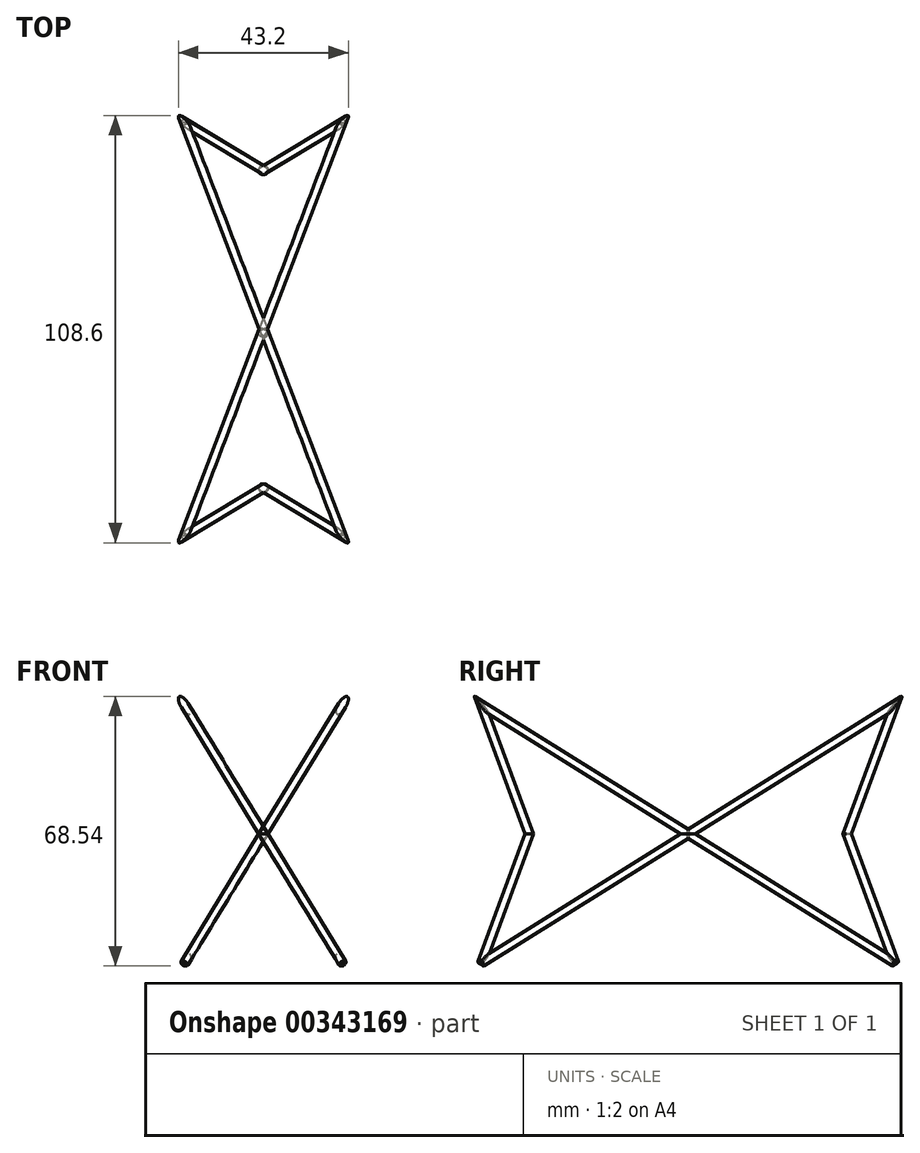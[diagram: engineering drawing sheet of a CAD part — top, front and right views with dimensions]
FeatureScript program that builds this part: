
annotation { "Feature Type Name" : "Feature", "Feature Type Description" : "" }
export const myFeature = defineFeature(function(context is Context, id is Id, definition is map)
    precondition{}
    {
        {
            var Q0;
            Q0=qCreatedBy(makeId("Right.planeOp"),FACE);
            var sketch = newSketch(context, id + "F0", { "sketchPlane" : qUnion([Q0])});
            skLineSegment(sketch, "E0", {"start": v(-52.44, 32.7) * mm, "end": v(52.44, -32.7) * mm, "construction": true});
            skLineSegment(sketch, "E1.MirrorCS", {"start": v(52.44, 32.7) * mm, "end": v(-52.44, -32.7) * mm, "construction": true});
            skLineSegment(sketch, "E2", {"start": v(-52.44, 32.7) * mm, "end": v(-40.37, 0) * mm, "construction": true});
            skLineSegment(sketch, "E3.MirrorCS", {"start": v(-52.44, -32.7) * mm, "end": v(-40.37, 0) * mm, "construction": true});
            skLineSegment(sketch, "E4.MirrorCS", {"start": v(52.44, 32.7) * mm, "end": v(40.37, 0) * mm, "construction": true});
            skLineSegment(sketch, "E5.MirrorCS", {"start": v(52.44, -32.7) * mm, "end": v(40.37, 0) * mm, "construction": true});
            skSolve(sketch);
        }
        {
            var Q0;
            Q0=qCreatedBy(makeId("Right.planeOp"),FACE);
            cPlane(context, id + "F1", {"entities" : qUnion([Q0]), "cplaneType" : CPlaneType.OFFSET, "offset" : 20 * mm, "width" : 150 * mm, "height" : 150 * mm});
        }
        {
            var Q0;
            Q0=qCreatedBy(makeId("Right.planeOp"),FACE);
            cPlane(context, id + "F2", {"entities" : qUnion([Q0]), "cplaneType" : CPlaneType.OFFSET, "offset" : 20 * mm, "oppositeDirection" : true, "width" : 150 * mm, "height" : 150 * mm});
        }
        {
            var Q0;
            Q0=qCreatedBy(id+"F1.planeOp",FACE);
            var sketch = newSketch(context, id + "F3", { "sketchPlane" : qUnion([Q0])});
            skLineSegment(sketch, "E6.0", {"start": v(52.44, 32.7) * mm, "end": v(-52.44, -32.7) * mm, "construction": true});
            skLineSegment(sketch, "E6.1", {"start": v(-52.44, -32.7) * mm, "end": v(-40.37, 0) * mm, "construction": true});
            skLineSegment(sketch, "E6.2", {"start": v(-52.44, 32.7) * mm, "end": v(-40.37, 0) * mm, "construction": true});
            skLineSegment(sketch, "E6.3", {"start": v(-52.44, 32.7) * mm, "end": v(52.44, -32.7) * mm, "construction": true});
            skLineSegment(sketch, "E6.4", {"start": v(52.44, -32.7) * mm, "end": v(40.37, 0) * mm, "construction": true});
            skLineSegment(sketch, "E6.5", {"start": v(52.44, 32.7) * mm, "end": v(40.37, 0) * mm, "construction": true});
            skSolve(sketch);
        }
        {
            var Q0;
            Q0=qCreatedBy(id+"F2.planeOp",FACE);
            var sketch = newSketch(context, id + "F4", { "sketchPlane" : qUnion([Q0])});
            skLineSegment(sketch, "E7.0", {"start": v(52.44, 32.7) * mm, "end": v(40.37, 0) * mm, "construction": true});
            skLineSegment(sketch, "E7.1", {"start": v(52.44, 32.7) * mm, "end": v(-52.44, -32.7) * mm, "construction": true});
            skLineSegment(sketch, "E7.2", {"start": v(52.44, -32.7) * mm, "end": v(40.37, 0) * mm, "construction": true});
            skLineSegment(sketch, "E7.3", {"start": v(-52.44, 32.7) * mm, "end": v(52.44, -32.7) * mm, "construction": true});
            skLineSegment(sketch, "E7.4", {"start": v(-52.44, 32.7) * mm, "end": v(-40.37, 0) * mm, "construction": true});
            skLineSegment(sketch, "E7.5", {"start": v(-52.44, -32.7) * mm, "end": v(-40.37, 0) * mm, "construction": true});
            skSolve(sketch);
        }
        {
            var Q0;
            Q0=sQuery(id+"F3.wireOp",EDGE,"E6.3");
            cPoint(context, id + "F5", {"entities" : qUnion([Q0]), "parameter" : 0.5});
        }
        {
            var Q0;
            Q0=sQuery(id+"F4.wireOp",VERTEX,"E7.1.start");
            var Q1;
            Q1=sQuery(id+"F0.wireOp",VERTEX,"E5.MirrorCS.end");
            var Q2;
            Q2 = qCreatedBy(id + "F5" ,VERTEX);
            cPlane(context, id + "F6", {"entities" : qUnion([Q0, Q1, Q2]), "cplaneType" : CPlaneType.THREE_POINT, "offset" : 25 * mm, "width" : 150 * mm, "height" : 150 * mm});
        }
        {
            var Q0;
            Q0=qCreatedBy(id+"F6.planeOp",FACE);
            var sketch = newSketch(context, id + "F7", { "sketchPlane" : qUnion([Q0])});
            skLineSegment(sketch, "E8", {"start": v(50, 37.93) * mm, "end": v(36.74, 0) * mm});
            skSolve(sketch);
        }
        {
            var Q0;
            Q0=sQuery(id+"F7.wireOp",VERTEX,"E8.end");
            var Q1;
            Q1=sQuery(id+"F4.wireOp",VERTEX,"E7.2.start");
            var Q2;
            Q2=sQuery(id+"F4.wireOp",VERTEX,"E7.2.end");
            cPlane(context, id + "F8", {"entities" : qUnion([Q0, Q1, Q2]), "cplaneType" : CPlaneType.THREE_POINT, "offset" : 25 * mm, "width" : 150 * mm, "height" : 150 * mm});
        }
        {
            var Q0;
            Q0=qCreatedBy(id+"F8.planeOp",FACE);
            var sketch = newSketch(context, id + "F9", { "sketchPlane" : qUnion([Q0])});
            skLineSegment(sketch, "E9", {"start": v(0, -13.98) * mm, "end": v(-20, -48.83) * mm});
            skSolve(sketch);
        }
        {
            var Q0;
            Q0=sQuery(id+"F3.wireOp",VERTEX,"E6.3.start");
            var Q1;
            Q1=sQuery(id+"F0.wireOp",VERTEX,"E2.end");
            var Q2;
            Q2=sQuery(id+"F3.wireOp",VERTEX,"E6.2.end");
            cPlane(context, id + "F10", {"entities" : qUnion([Q0, Q1, Q2]), "cplaneType" : CPlaneType.THREE_POINT, "offset" : 25 * mm, "width" : 150 * mm, "height" : 150 * mm});
        }
        {
            var Q0;
            Q0=qCreatedBy(id+"F10.planeOp",FACE);
            var sketch = newSketch(context, id + "F11", { "sketchPlane" : qUnion([Q0])});
            skLineSegment(sketch, "E10", {"start": v(-20, 48.83) * mm, "end": v(0, 13.98) * mm});
            skSolve(sketch);
        }
        {
            var Q0;
            Q0=sQuery(id+"F11.wireOp",VERTEX,"E10.end");
            var Q1;
            Q1=sQuery(id+"F3.wireOp",VERTEX,"E6.2.end");
            var Q2;
            Q2=sQuery(id+"F3.wireOp",VERTEX,"E6.1.start");
            cPlane(context, id + "F12", {"entities" : qUnion([Q0, Q1, Q2]), "cplaneType" : CPlaneType.THREE_POINT, "offset" : 25 * mm, "width" : 150 * mm, "height" : 150 * mm});
        }
        {
            var Q0;
            Q0=qCreatedBy(id+"F12.planeOp",FACE);
            var sketch = newSketch(context, id + "F13", { "sketchPlane" : qUnion([Q0])});
            skLineSegment(sketch, "E11", {"start": v(0, -13.98) * mm, "end": v(20, -48.83) * mm});
            skSolve(sketch);
        }
        {
            var Q0;
            Q0=sQuery(id+"F11.wireOp",VERTEX,"E10.start");
            var Q1;
            Q1=sQuery(id+"F13.wireOp",VERTEX,"E11.end");
            var Q2;
            Q2=sQuery(id+"F7.wireOp",VERTEX,"E8.start");
            cPlane(context, id + "F14", {"entities" : qUnion([Q0, Q1, Q2]), "cplaneType" : CPlaneType.THREE_POINT, "offset" : 25 * mm, "width" : 150 * mm, "height" : 150 * mm});
        }
        {
            var Q0;
            Q0=qCreatedBy(id+"F14.planeOp",FACE);
            var sketch = newSketch(context, id + "F15", { "sketchPlane" : qUnion([Q0])});
            skLineSegment(sketch, "E12", {"start": v(56.12, -32.7) * mm, "end": v(-56.12, 32.7) * mm});
            skSolve(sketch);
        }
        {
            var Q0;
            Q0=sQuery(id+"F11.wireOp",VERTEX,"E10.start");
            var Q1;
            Q1=sQuery(id+"F15.wireOp",VERTEX,"E12.start");
            var Q2;
            Q2=sQuery(id+"F9.wireOp",VERTEX,"E9.end");
            cPlane(context, id + "F16", {"entities" : qUnion([Q0, Q1, Q2]), "cplaneType" : CPlaneType.THREE_POINT, "offset" : 25 * mm, "width" : 150 * mm, "height" : 150 * mm});
        }
        {
            var Q0;
            Q0=qCreatedBy(id+"F16.planeOp",FACE);
            var sketch = newSketch(context, id + "F17", { "sketchPlane" : qUnion([Q0])});
            skLineSegment(sketch, "E13", {"start": v(56.12, 32.7) * mm, "end": v(-56.12, -32.7) * mm});
            skSolve(sketch);
        }
        {
            var Q0;
            Q0=sQuery(id+"F17.wireOp",EDGE,"E13");
            var Q1;
            Q1=sQuery(id+"F17.wireOp",VERTEX,"E13.end");
            cPlane(context, id + "F18", {"entities" : qUnion([Q0, Q1]), "cplaneType" : CPlaneType.LINE_POINT, "offset" : 25 * mm, "width" : 150 * mm, "height" : 150 * mm});
        }
        {
            var Q0;
            Q0=qCreatedBy(id+"F18.planeOp",FACE);
            var sketch = newSketch(context, id + "F19", { "sketchPlane" : qUnion([Q0])});
            skCircle(sketch, "E14", {"center": v(0, 0) * mm, "radius": 1 * mm});
            skSolve(sketch);
        }
        {
            var Q0;
            Q0=makeQuery(id+"F19.imprint","IMPRINT",FACE,{"disambiguationData":[TD([[makeQuery(id+"F19.imprint","IMPRINT",EDGE,{"derivedFrom":sQuery(id+"F19.wireOp",EDGE,"E14")}),1.0]])]});
            var Q1;
            Q1=sQuery(id+"F17.wireOp",EDGE,"E13");
            var Q2;
            Q2=sQuery(id+"F11.wireOp",EDGE,"E10");
            var Q3;
            Q3=sQuery(id+"F13.wireOp",EDGE,"E11");
            sweep(context, id + "F20", {"profiles" : qUnion([Q0]), "path" : qUnion([Q1, Q2, Q3])});
        }
        {
            var Q0;
            Q0=sQuery(id+"F9.wireOp",EDGE,"E9");
            var Q1;
            Q1=sQuery(id+"F9.wireOp",VERTEX,"E9.end");
            cPlane(context, id + "F21", {"entities" : qUnion([Q0, Q1]), "cplaneType" : CPlaneType.LINE_POINT, "offset" : 25 * mm, "width" : 150 * mm, "height" : 150 * mm});
        }
        {
            var Q0;
            Q0=qCreatedBy(id+"F21.planeOp",FACE);
            var sketch = newSketch(context, id + "F22", { "sketchPlane" : qUnion([Q0])});
            skCircle(sketch, "E15", {"center": v(6.96, -37.87) * mm, "radius": 1 * mm});
            skSolve(sketch);
        }
        {
            var Q0;
            Q0=makeQuery(id+"F22.imprint","IMPRINT",FACE,{"disambiguationData":[TD([[makeQuery(id+"F22.imprint","IMPRINT",EDGE,{"derivedFrom":sQuery(id+"F22.wireOp",EDGE,"E15")}),1.0]])]});
            var Q1;
            Q1=sQuery(id+"F9.wireOp",EDGE,"E9");
            var Q2;
            Q2=sQuery(id+"F7.wireOp",EDGE,"E8");
            var Q3;
            Q3=sQuery(id+"F15.wireOp",EDGE,"E12");
            sweep(context, id + "F23", {"operationType" : NewBodyOperationType.ADD, "profiles" : qUnion([Q0]), "path" : qUnion([Q1, Q2, Q3])});
        }
        {
            var Q0;
            Q0=makeQuery(id+"F20.opSweep","SWEPT_BODY",BODY,{"disambiguationData":[OSD([sQuery(id+"F13.wireOp",EDGE,"E11"),sQuery(id+"F19.wireOp",EDGE,"E14")])]});
            var Q1;
            Q1=qCreatedBy(makeId("Right.planeOp"),FACE);
            mirror(context, id + "F24", {"entities" : qUnion([Q0]), "mirrorPlane" : qUnion([Q1])});
        }
    });
